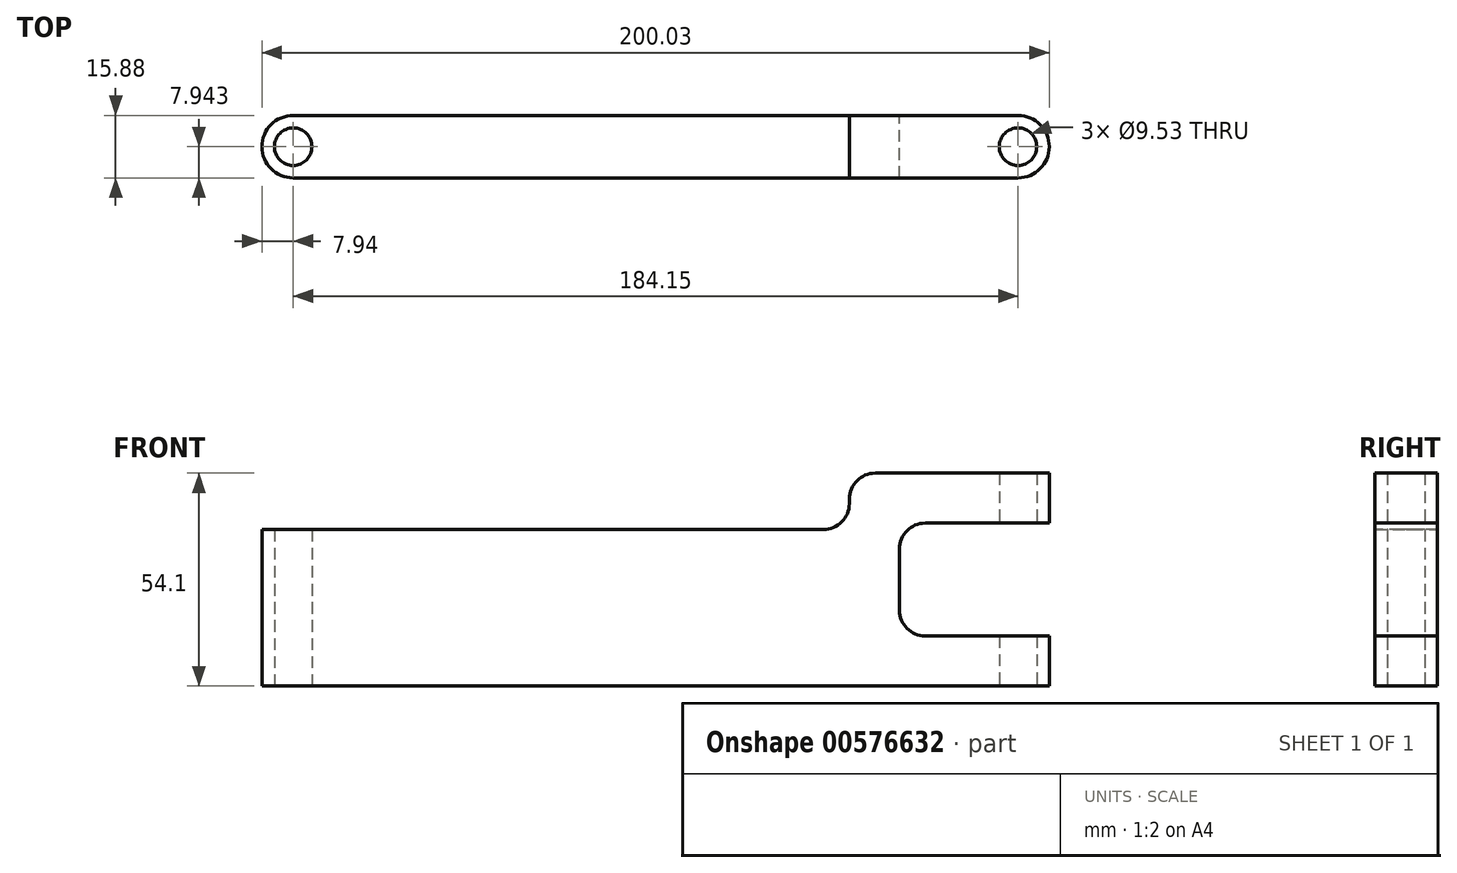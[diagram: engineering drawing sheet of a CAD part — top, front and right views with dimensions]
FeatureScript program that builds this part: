
annotation { "Feature Type Name" : "Feature", "Feature Type Description" : "" }
export const myFeature = defineFeature(function(context is Context, id is Id, definition is map)
    precondition{}
    {
        {
            var Q0;
            Q0=qCreatedBy(makeId("Top.planeOp"),FACE);
            var sketch = newSketch(context, id + "F0", { "sketchPlane" : qUnion([Q0])});
            skLineSegment(sketch, "E0.bottom", {"start": v(0, 0) * mm, "end": v(184.15, 0) * mm});
            skLineSegment(sketch, "E0.top", {"start": v(0, -15.88) * mm, "end": v(184.15, -15.88) * mm});
            skLineSegment(sketch, "E0.left", {"start": v(0, 0) * mm, "end": v(0, -15.88) * mm});
            skLineSegment(sketch, "E0.right", {"start": v(184.15, 0) * mm, "end": v(184.15, -15.88) * mm});
            skCircle(sketch, "E1", {"center": v(0, -7.94) * mm, "radius": 7.94 * mm});
            skCircle(sketch, "E2", {"center": v(184.15, -7.94) * mm, "radius": 7.94 * mm});
            skSolve(sketch);
        }
        {
            var Q0;
            {var subQ0=sQuery(id+"F0.wireOp",EDGE,"E0.right");Q0=makeQuery(id+"F0.imprint","IMPRINT",FACE,{"disambiguationData":[TD([[makeQuery(id+"F0.imprint","IMPRINT",EDGE,{"derivedFrom":subQ0}),1.0]])]});}
            var Q1;
            {var subQ0=sQuery(id+"F0.wireOp",EDGE,"E0.right");Q1=makeQuery(id+"F0.imprint","IMPRINT",FACE,{"disambiguationData":[TD([[makeQuery(id+"F0.imprint","IMPRINT",EDGE,{"derivedFrom":subQ0}),-1.0]])]});}
            var Q2;
            {var subQ0=sQuery(id+"F0.wireOp",EDGE,"E0.bottom");Q2=makeQuery(id+"F0.imprint","IMPRINT",FACE,{"disambiguationData":[TD([[makeQuery(id+"F0.imprint","IMPRINT",EDGE,{"derivedFrom":subQ0}),-1.0]])]});}
            var Q3;
            {var subQ0=sQuery(id+"F0.wireOp",EDGE,"E0.left");Q3=makeQuery(id+"F0.imprint","IMPRINT",FACE,{"disambiguationData":[TD([[makeQuery(id+"F0.imprint","IMPRINT",EDGE,{"derivedFrom":subQ0}),1.0]])]});}
            var Q4;
            {var subQ0=sQuery(id+"F0.wireOp",EDGE,"E0.left");Q4=makeQuery(id+"F0.imprint","IMPRINT",FACE,{"disambiguationData":[TD([[makeQuery(id+"F0.imprint","IMPRINT",EDGE,{"derivedFrom":subQ0}),-1.0]])]});}
            extrude(context, id + "F1", {"entities" : qUnion([Q0, Q1, Q2, Q3, Q4]), "depth" : 54.1 * mm, "offsetDistance" : 25.4 * mm});
        }
        {
            var Q0;
            Q0=sQuery(id+"F0.wireOp",VERTEX,"E1.center");
            var Q1;
            Q1=sQuery(id+"F0.wireOp",VERTEX,"E2.center");
            var Q2;
            Q2=makeQuery(id+"F1.opExtrude","SWEPT_BODY",BODY,{"disambiguationData":[OSD([sQuery(id+"F0.wireOp",EDGE,"E0.bottom"),sQuery(id+"F0.wireOp",EDGE,"E0.top"),sQuery(id+"F0.wireOp",EDGE,"E1"),sQuery(id+"F0.wireOp",EDGE,"E2")])]});
            hole(context, id + "F2", {"style" : HoleStyle.SIMPLE, "endStyle" : HoleEndStyle.THROUGH, "oppositeDirection" : true, "holeDiameter" : 9.52 * mm, "isTappedThrough" : true, "tappedDepth" : 12.7 * mm, "tapClearance" : 3, "locations" : qUnion([Q0, Q1]), "scope" : qUnion([Q2])});
        }
        {
            var Q0;
            Q0=qCreatedBy(makeId("Front.planeOp"),FACE);
            var sketch = newSketch(context, id + "F3", { "sketchPlane" : qUnion([Q0])});
            skLineSegment(sketch, "E3.bottom", {"start": v(153.99, 41.4) * mm, "end": v(217.49, 41.4) * mm});
            skLineSegment(sketch, "E3.top", {"start": v(153.99, 12.7) * mm, "end": v(217.49, 12.7) * mm});
            skLineSegment(sketch, "E3.left", {"start": v(153.99, 41.4) * mm, "end": v(153.99, 12.7) * mm});
            skLineSegment(sketch, "E3.right", {"start": v(217.49, 41.4) * mm, "end": v(217.49, 12.7) * mm});
            skLineSegment(sketch, "E4", {"start": v(-7.94, 0) * mm, "end": v(-7.94, 54.1) * mm});
            skLineSegment(sketch, "E5", {"start": v(-7.94, 27.05) * mm, "end": v(280.11, 27.05) * mm, "construction": true});
            skLineSegment(sketch, "E6.0", {"start": v(0, 54.1) * mm, "end": v(-7.94, 54.1) * mm});
            skLineSegment(sketch, "E7", {"start": v(192.09, 54.1) * mm, "end": v(192.09, 0) * mm});
            skSolve(sketch);
        }
        {
            var Q0;
            {var subQ0=sQuery(id+"F3.wireOp",EDGE,"E3.right");Q0=makeQuery(id+"F3.imprint","IMPRINT",FACE,{"disambiguationData":[TD([[makeQuery(id+"F3.imprint","IMPRINT",EDGE,{"derivedFrom":subQ0}),-1.0]])]});}
            var Q1;
            {var subQ0=sQuery(id+"F3.wireOp",EDGE,"E3.left");Q1=makeQuery(id+"F3.imprint","IMPRINT",FACE,{"disambiguationData":[TD([[makeQuery(id+"F3.imprint","IMPRINT",EDGE,{"derivedFrom":subQ0}),1.0]])]});}
            extrude(context, id + "F4", {"entities" : qUnion([Q0, Q1]), "operationType" : NewBodyOperationType.REMOVE, "depth" : 25.4 * mm, "offsetDistance" : 25.4 * mm});
        }
        {
            var Q0;
            Q0=makeQuery(id+"F4.boolean.opBoolean","COPY",EDGE,{"derivedFrom":makeQuery(id+"F4.opExtrude","SWEPT_EDGE",EDGE,{"disambiguationData":[OSD([sQuery(id+"F3.wireOp",EDGE,"E3.bottom"),sQuery(id+"F3.wireOp",EDGE,"E3.left")])]})});
            var Q1;
            Q1=makeQuery(id+"F4.boolean.opBoolean","COPY",EDGE,{"derivedFrom":makeQuery(id+"F4.opExtrude","SWEPT_EDGE",EDGE,{"disambiguationData":[OSD([sQuery(id+"F3.wireOp",EDGE,"E3.top"),sQuery(id+"F3.wireOp",EDGE,"E3.left")])]})});
            fillet(context, id + "F5", {"entities" : qUnion([Q0, Q1]), "radius" : 6.6 * mm, "tangentPropagation" : true, "allowEdgeOverflow" : false});
        }
        {
            var Q0;
            Q0=qCreatedBy(makeId("Front.planeOp"),FACE);
            var sketch = newSketch(context, id + "F6", { "sketchPlane" : qUnion([Q0])});
            skLineSegment(sketch, "E8", {"start": v(-7.94, 0) * mm, "end": v(-7.94, 54.1) * mm});
            skLineSegment(sketch, "E9.0", {"start": v(-7.94, 0) * mm, "end": v(7.94, 0) * mm});
            skLineSegment(sketch, "E10.0", {"start": v(0, 54.1) * mm, "end": v(-7.94, 54.1) * mm});
            skLineSegment(sketch, "E11", {"start": v(-7.94, 27.05) * mm, "end": v(260.06, 27.05) * mm, "construction": true});
            skLineSegment(sketch, "E12.0.0", {"start": v(184.15, 41.4) * mm, "end": v(160.6, 41.4) * mm});
            skArc(sketch, "E12.0.1", {"start": v(160.6, 41.4) * mm, "mid": v(155.92, 39.47) * mm, "end": v(153.99, 34.8) * mm});
            skLineSegment(sketch, "E12.0.2", {"start": v(153.99, 34.8) * mm, "end": v(153.99, 19.3) * mm});
            skArc(sketch, "E12.0.3", {"start": v(153.99, 19.3) * mm, "mid": v(155.92, 14.63) * mm, "end": v(160.6, 12.7) * mm});
            skLineSegment(sketch, "E12.0.4", {"start": v(160.6, 12.7) * mm, "end": v(184.15, 12.7) * mm});
            skLineSegment(sketch, "E12.0.5", {"start": v(184.15, 12.7) * mm, "end": v(184.15, 0) * mm});
            skLineSegment(sketch, "E12.0.6", {"start": v(184.15, 0) * mm, "end": v(0, 0) * mm});
            skLineSegment(sketch, "E12.0.7", {"start": v(0, 0) * mm, "end": v(0, 54.1) * mm});
            skLineSegment(sketch, "E12.0.8", {"start": v(0, 54.1) * mm, "end": v(184.15, 54.1) * mm});
            skLineSegment(sketch, "E12.0.9", {"start": v(184.15, 54.1) * mm, "end": v(184.15, 41.4) * mm});
            skLineSegment(sketch, "E13.bottom", {"start": v(-20.64, 39.75) * mm, "end": v(141.29, 39.75) * mm});
            skLineSegment(sketch, "E13.top", {"start": v(-20.64, 66.8) * mm, "end": v(141.29, 66.8) * mm});
            skLineSegment(sketch, "E13.left", {"start": v(-20.64, 39.75) * mm, "end": v(-20.64, 66.8) * mm});
            skLineSegment(sketch, "E13.right", {"start": v(141.29, 39.75) * mm, "end": v(141.29, 66.8) * mm});
            skSolve(sketch);
        }
        {
            var Q0;
            {var subQ3=sQuery(id+"F6.wireOp",EDGE,"E13.bottom");var subQ5=sQuery(id+"F6.wireOp",EDGE,"E13.right");var subQ7=makeQuery(id+"F6.imprint","INTERSECT",VERTEX,{"derivedFrom":[subQ3,subQ5]});Q0=makeQuery(id+"F6.imprint","IMPRINT",FACE,{"disambiguationData":[TD([[makeQuery(id+"F6.imprint","IMPRINT",EDGE,{"disambiguationData":[TD([[subQ7,1.0]])],"derivedFrom":subQ3}),1.0]])]});}
            var Q1;
            {var subQ0=sQuery(id+"F6.wireOp",EDGE,"E10.0");Q1=makeQuery(id+"F6.imprint","IMPRINT",FACE,{"disambiguationData":[TD([[makeQuery(id+"F6.imprint","IMPRINT",EDGE,{"derivedFrom":subQ0}),1.0]])]});}
            var Q2;
            {var subQ1=sQuery(id+"F6.wireOp",EDGE,"E10.0");Q2=makeQuery(id+"F6.imprint","IMPRINT",FACE,{"disambiguationData":[TD([[makeQuery(id+"F6.imprint","IMPRINT",EDGE,{"derivedFrom":subQ1}),-1.0]])]});}
            extrude(context, id + "F7", {"entities" : qUnion([Q0, Q1, Q2]), "operationType" : NewBodyOperationType.REMOVE, "depth" : 25.4 * mm, "offsetDistance" : 25.4 * mm});
        }
        {
            var Q0;
            Q0=makeQuery(id+"F1.opExtrude","CAP_FACE",FACE,{"disambiguationData":[OSD([sQuery(id+"F0.wireOp",EDGE,"E0.bottom"),sQuery(id+"F0.wireOp",EDGE,"E0.top"),sQuery(id+"F0.wireOp",EDGE,"E1"),sQuery(id+"F0.wireOp",EDGE,"E2")])],"isStart":false});
            var Q1;
            {var subQ0=sQuery(id+"F0.wireOp",EDGE,"E0.bottom");Q1=makeQuery(id+"F0.imprint","IMPRINT",FACE,{"disambiguationData":[TD([[makeQuery(id+"F0.imprint","IMPRINT",EDGE,{"derivedFrom":subQ0}),-1.0]])]});}
            cPlane(context, id + "F8", {"entities" : qUnion([Q0, Q1]), "cplaneType" : CPlaneType.MID_PLANE, "offset" : 25.4 * mm, "width" : 152.4 * mm, "height" : 152.4 * mm});
        }
        {
            var Q0;
            Q0=makeQuery(id+"F7.boolean.opBoolean","COPY",EDGE,{"derivedFrom":makeQuery(id+"F7.opExtrude","SWEPT_EDGE",EDGE,{"disambiguationData":[OSD([sQuery(id+"F6.wireOp",EDGE,"E13.bottom"),sQuery(id+"F6.wireOp",EDGE,"E13.right")])]})});
            var Q1;
            Q1=makeQuery(id+"F7.boolean.opBoolean","INTERSECT",EDGE,{"derivedFrom":[makeQuery(id+"F1.opExtrude","CAP_FACE",FACE,{"disambiguationData":[OSD([sQuery(id+"F0.wireOp",EDGE,"E0.bottom"),sQuery(id+"F0.wireOp",EDGE,"E0.top"),sQuery(id+"F0.wireOp",EDGE,"E1"),sQuery(id+"F0.wireOp",EDGE,"E2")])],"isStart":false}),makeQuery(id+"F7.opExtrude","SWEPT_FACE",FACE,{"disambiguationData":[OSD([sQuery(id+"F6.wireOp",EDGE,"E13.right")])]})]});
            var Q2;
            Q2=makeQuery(id+"FNxyIRRoFIMBhzE_1.1.F7.boolean.opBoolean","COPY",EDGE,{"derivedFrom":makeQuery(id+"FNxyIRRoFIMBhzE_1.1.F7.opExtrude","SWEPT_EDGE",EDGE,{"disambiguationData":[OSD([sQuery(id+"F6.wireOp",EDGE,"E13.bottom"),sQuery(id+"F6.wireOp",EDGE,"E13.right")])]})});
            var Q3;
            Q3=makeQuery(id+"FNxyIRRoFIMBhzE_1.1.F7.boolean.opBoolean","INTERSECT",EDGE,{"derivedFrom":[makeQuery(id+"F1.opExtrude","CAP_FACE",FACE,{"disambiguationData":[OSD([sQuery(id+"F0.wireOp",EDGE,"E0.bottom"),sQuery(id+"F0.wireOp",EDGE,"E0.top"),sQuery(id+"F0.wireOp",EDGE,"E1"),sQuery(id+"F0.wireOp",EDGE,"E2")])],"isStart":true}),makeQuery(id+"FNxyIRRoFIMBhzE_1.1.F7.opExtrude","SWEPT_FACE",FACE,{"disambiguationData":[OSD([sQuery(id+"F6.wireOp",EDGE,"E13.right")])]})]});
            fillet(context, id + "F9", {"entities" : qUnion([Q0, Q1, Q2, Q3]), "radius" : 6.6 * mm, "tangentPropagation" : true, "allowEdgeOverflow" : false});
        }
    });
